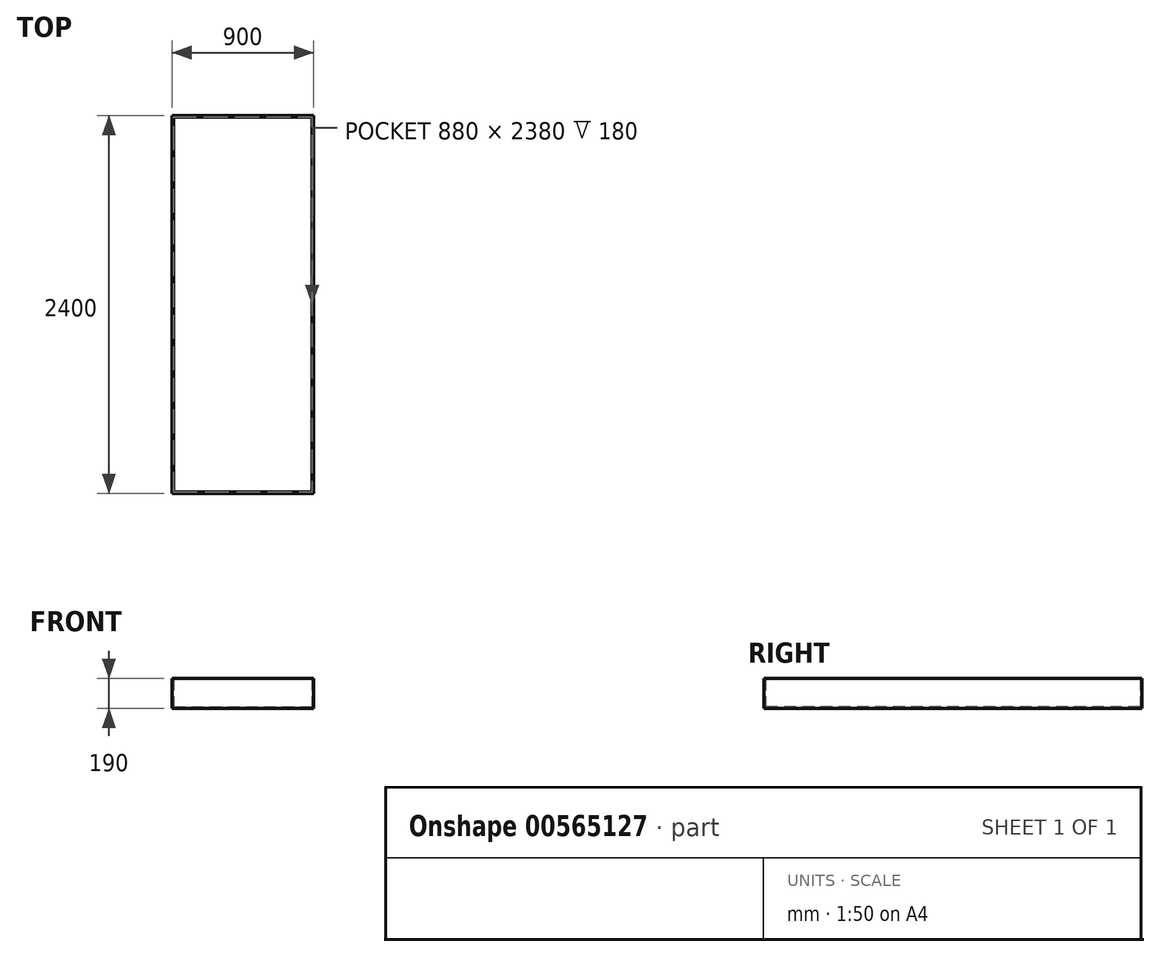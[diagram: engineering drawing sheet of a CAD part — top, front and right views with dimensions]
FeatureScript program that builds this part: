
annotation { "Feature Type Name" : "Feature", "Feature Type Description" : "" }
export const myFeature = defineFeature(function(context is Context, id is Id, definition is map)
    precondition{}
    {
        {
            var Q0;
            Q0=qCreatedBy(makeId("Top.planeOp"),FACE);
            var sketch = newSketch(context, id + "F0", { "sketchPlane" : qUnion([Q0])});
            skLineSegment(sketch, "E0.bottom", {"start": v(-450, 1200) * mm, "end": v(450, 1200) * mm});
            skLineSegment(sketch, "E0.top", {"start": v(-450, -1200) * mm, "end": v(450, -1200) * mm});
            skLineSegment(sketch, "E0.left", {"start": v(-450, 1200) * mm, "end": v(-450, -1200) * mm});
            skLineSegment(sketch, "E0.right", {"start": v(450, 1200) * mm, "end": v(450, -1200) * mm});
            skSolve(sketch);
        }
        {
            var Q0;
            Q0=makeQuery(id+"F0.imprint","IMPRINT",FACE,{"disambiguationData":[TD([[makeQuery(id+"F0.imprint","IMPRINT",EDGE,{"derivedFrom":sQuery(id+"F0.wireOp",EDGE,"E0.bottom")}),-1.0]])]});
            extrude(context, id + "F1", {"entities" : qUnion([Q0]), "depth" : 10 * mm, "offsetDistance" : 25 * mm});
        }
        {
            var Q0;
            Q0=makeQuery(id+"F1.opExtrude","CAP_FACE",FACE,{"disambiguationData":[OSD([sQuery(id+"F0.wireOp",EDGE,"E0.bottom"),sQuery(id+"F0.wireOp",EDGE,"E0.top"),sQuery(id+"F0.wireOp",EDGE,"E0.left"),sQuery(id+"F0.wireOp",EDGE,"E0.right")])],"isStart":false});
            var sketch = newSketch(context, id + "F2", { "sketchPlane" : qUnion([Q0])});
            skLineSegment(sketch, "E1.bottom", {"start": v(-450, 1200) * mm, "end": v(450, 1200) * mm});
            skLineSegment(sketch, "E1.top", {"start": v(-450, -1200) * mm, "end": v(450, -1200) * mm});
            skLineSegment(sketch, "E1.left", {"start": v(-450, 1200) * mm, "end": v(-450, -1200) * mm});
            skLineSegment(sketch, "E1.right", {"start": v(450, 1200) * mm, "end": v(450, -1200) * mm});
            skLineSegment(sketch, "E2.bottom", {"start": v(-440, 1190) * mm, "end": v(440, 1190) * mm});
            skLineSegment(sketch, "E2.top", {"start": v(-440, -1190) * mm, "end": v(440, -1190) * mm});
            skLineSegment(sketch, "E2.left", {"start": v(-440, 1190) * mm, "end": v(-440, -1190) * mm});
            skLineSegment(sketch, "E2.right", {"start": v(440, 1190) * mm, "end": v(440, -1190) * mm});
            skSolve(sketch);
        }
        {
            var Q0;
            Q0=makeQuery(id+"F2.imprint","IMPRINT",FACE,{"disambiguationData":[TD([[makeQuery(id+"F2.imprint","IMPRINT",EDGE,{"derivedFrom":sQuery(id+"F2.wireOp",EDGE,"E1.bottom")}),-1.0]])]});
            extrude(context, id + "F3", {"entities" : qUnion([Q0]), "operationType" : NewBodyOperationType.ADD, "depth" : 180 * mm, "offsetDistance" : 25 * mm});
        }
    });
